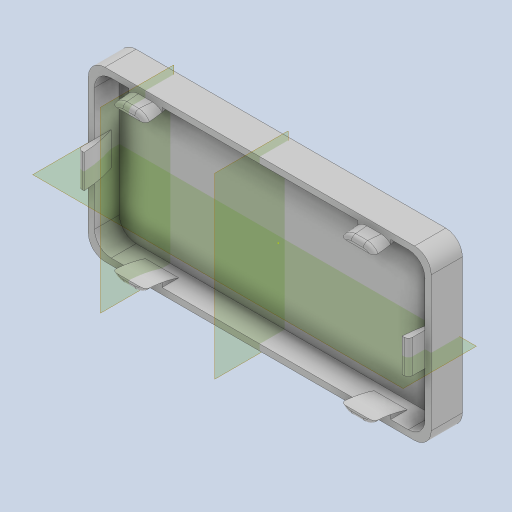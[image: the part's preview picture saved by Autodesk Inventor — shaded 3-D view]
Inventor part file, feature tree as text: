
AUTODESK INVENTOR PART (.ipt)
format: ipt  version: 2024 (Build 280153000, 153)  size: 412,672 bytes
history: native  units: mm
features: fillet x9, sketch x8, extrude x7, other x6, mirror x6, plane x3
ambient origin geometry x8: Origin, YZ Plane, XZ Plane, XY Plane, X Axis, Y Axis, Z Axis, Center Point
bodies: Body1 (feature_tree)
feature tree (39):
  other  "Sólido1"
  extrude  "Extrusión1"  Depth=1.5mm
  extrude  "Extrusión2"  Depth=14.0mm
  extrude  "Extrusión3"  Depth=20.75mm
  fillet  "Empalme1"  Radius=13.75mm
  plane  "Plano de trabajo1"
  plane  "Plano de trabajo2"
  extrude  "Extrusión4"  Depth=2.0mm
  fillet  "Empalme2"  Radius=16.0mm
  mirror  "Simetría1"
  mirror  "Simetría2"
  fillet  "Empalme3"  Radius=2.0mm
  sketch  "Boceto5"  dims[d17=39.75mm d18=18.75mm d24=8.0mm d25=30.0mm]
  extrude  "Extrusión5"  Depth=18.75mm
  fillet  "Empalme4"  Radius=8.0mm
  fillet  "Empalme5"  Radius=30.0mm
  mirror  "Simetría3"
  extrude  "Extrusión6"  Depth=8.0mm TaperAngle=0.0deg
  fillet  "Empalme6"  Radius=2.0mm
  fillet  "Empalme7"  Radius=4.0mm
  mirror  "Simetría4"
  plane  "Plano de trabajo3"
  extrude  "Extrusión7"  Depth=8.0mm
  fillet  "Empalme8"  Radius=30.0mm
  fillet  "Empalme9"  Radius=8.0mm
  mirror  "Simetría5"
  mirror  "Simetría6"
  sketch  "Boceto1"  dims[d4=0.0mm d5=1.5mm]
  sketch  "Boceto2"  dims[d6=6.0mm d7=0.0mm d8=14.0mm]
  sketch  "Boceto3"  dims[d9=9.0mm d10=20.75mm d11=13.75mm]
  sketch  "Boceto4"  dims[d12=12.75mm d13=2.0mm d14=16.0mm d15=0.0mm d16=2.0mm]
  sketch  "Boceto6"  dims[d26=1.5mm d27=8.0mm d28=0.0mm d29=2.0mm d30=4.0mm]
  sketch  "Boceto7"  dims[d31=1.5mm d32=8.0mm d33=30.0mm d34=8.0mm d35=0.0mm]
  sketch  "Boceto8"  dims[d36=3.0mm d37=1.0mm d38=1.5mm d39=8.0mm d40=30.0mm d41=8.0mm d42=0.0mm d43=3.0mm d44=1.0mm d45=27.5mm d46=1.5mm d47=8.0mm d48=30.0mm d49=1.5mm d50=8.0mm d51=0.0mm d52=3.0mm d53=1.0mm]
  other  "Proyectar aristas de corte1"
  other  "Proyectar aristas de corte2"
  other  "Proyectar aristas de corte3"
  other  "Proyectar aristas de corte4"
  other  "Proyectar aristas de corte5"
